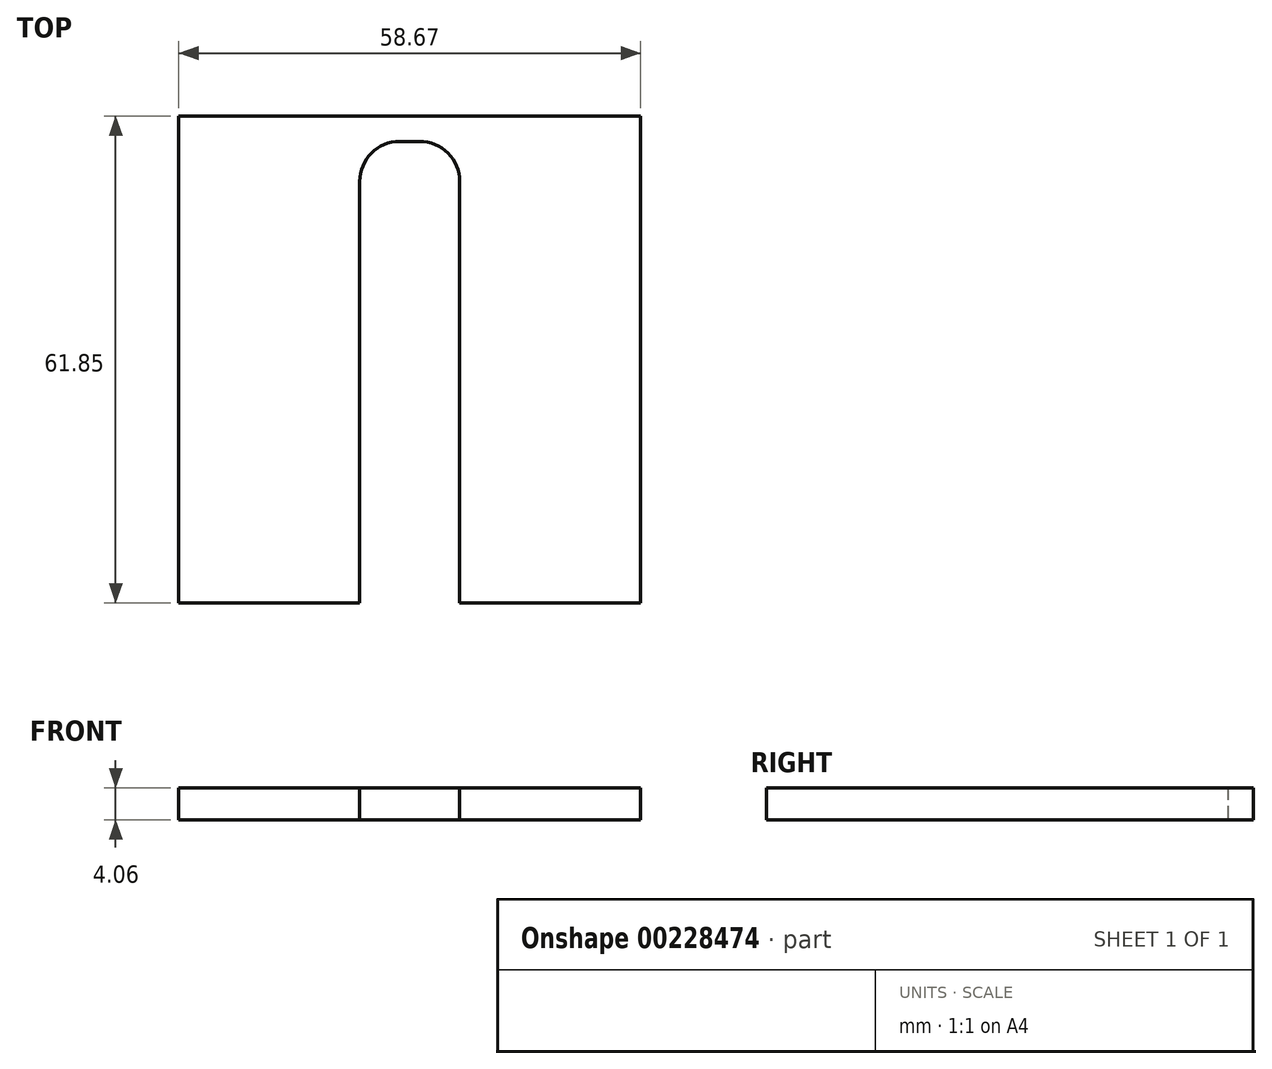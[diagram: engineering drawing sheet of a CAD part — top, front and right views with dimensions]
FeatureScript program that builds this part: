
annotation { "Feature Type Name" : "Feature", "Feature Type Description" : "" }
export const myFeature = defineFeature(function(context is Context, id is Id, definition is map)
    precondition{}
    {
        {
            var Q0;
            Q0=qCreatedBy(makeId("Top.planeOp"),FACE);
            var sketch = newSketch(context, id + "F0", { "sketchPlane" : qUnion([Q0])});
            skLineSegment(sketch, "E0", {"start": v(-62.25, 28.87) * mm, "end": v(-3.58, 28.87) * mm});
            skLineSegment(sketch, "E1", {"start": v(-62.25, 28.87) * mm, "end": v(-62.25, -32.98) * mm});
            skLineSegment(sketch, "E2", {"start": v(-3.58, 28.87) * mm, "end": v(-3.58, -32.98) * mm});
            skLineSegment(sketch, "E3.0", {"start": v(-39.27, 25.65) * mm, "end": v(-39.27, -32.98) * mm});
            skLineSegment(sketch, "E4.0", {"start": v(-26.57, 25.65) * mm, "end": v(-26.57, -32.98) * mm});
            skLineSegment(sketch, "E5", {"start": v(-39.27, 25.65) * mm, "end": v(-26.57, 25.65) * mm});
            skLineSegment(sketch, "E6", {"start": v(-62.25, -32.98) * mm, "end": v(-39.27, -32.98) * mm});
            skLineSegment(sketch, "E7", {"start": v(-26.57, -32.98) * mm, "end": v(-3.58, -32.98) * mm});
            skSolve(sketch);
        }
        {
            var Q0;
            Q0=makeQuery(id+"F0.imprint","IMPRINT",FACE,{"disambiguationData":[TD([[makeQuery(id+"F0.imprint","IMPRINT",EDGE,{"derivedFrom":sQuery(id+"F0.wireOp",EDGE,"E0")}),-1.0]])]});
            extrude(context, id + "F1", {"entities" : qUnion([Q0]), "depth" : 4.06 * mm});
        }
        {
            var Q0;
            Q0=makeQuery(id+"F1.opExtrude","SWEPT_EDGE",EDGE,{"disambiguationData":[OSD([sQuery(id+"F0.wireOp",EDGE,"E3.0"),sQuery(id+"F0.wireOp",EDGE,"E5")])]});
            var Q1;
            Q1=makeQuery(id+"F1.opExtrude","SWEPT_EDGE",EDGE,{"disambiguationData":[OSD([sQuery(id+"F0.wireOp",EDGE,"E4.0"),sQuery(id+"F0.wireOp",EDGE,"E5")])]});
            fillet(context, id + "F2", {"entities" : qUnion([Q0, Q1]), "radius" : 5.08 * mm, "tangentPropagation" : true, "allowEdgeOverflow" : false});
        }
    });
